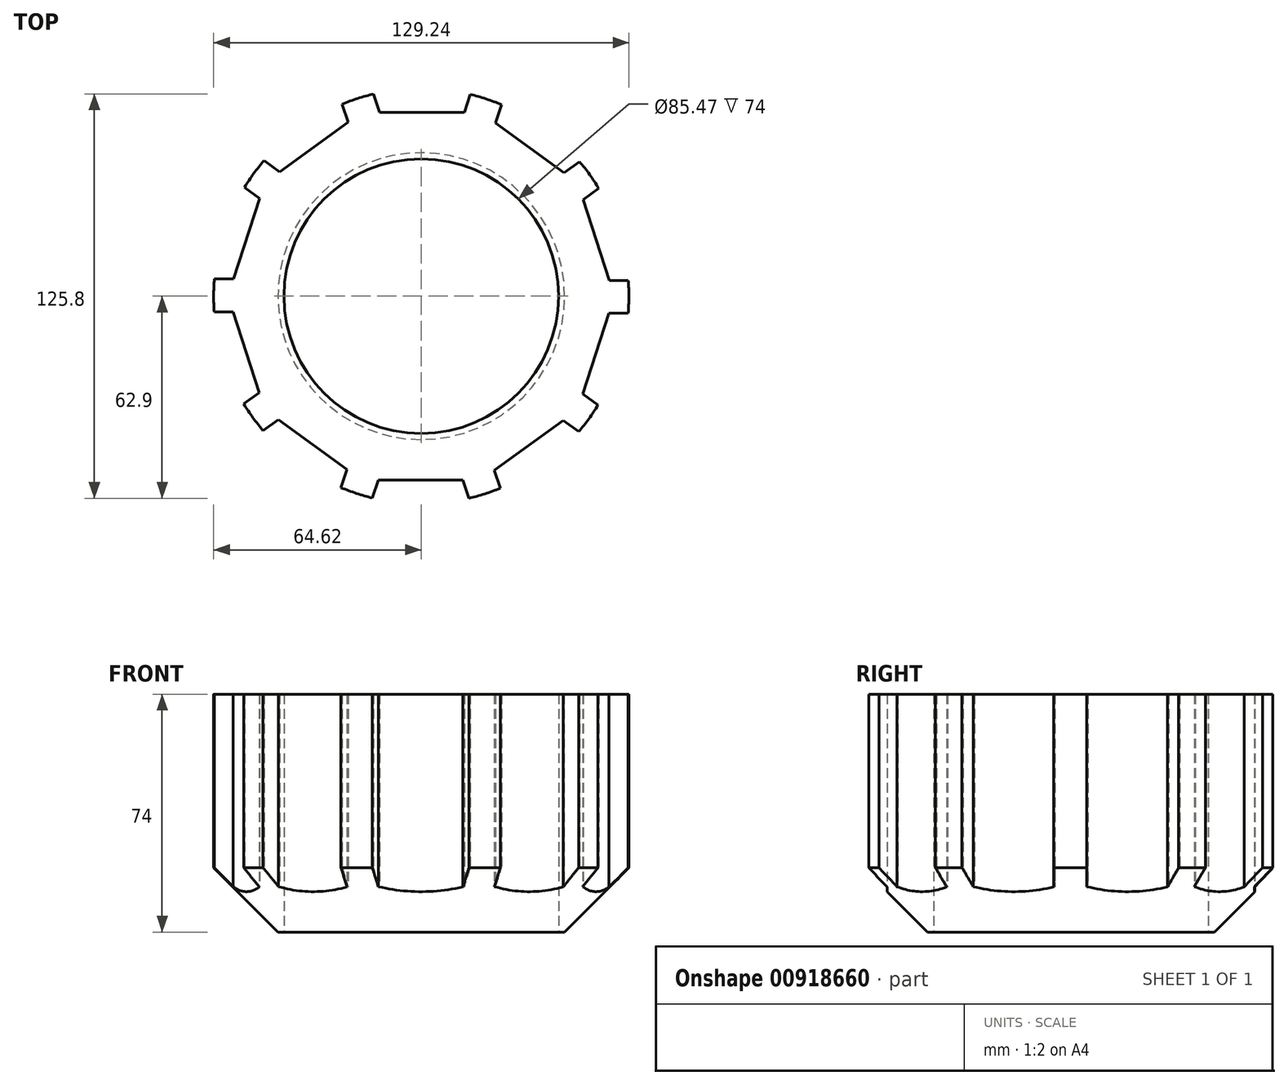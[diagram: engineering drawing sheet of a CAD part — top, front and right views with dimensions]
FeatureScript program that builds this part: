
annotation { "Feature Type Name" : "Feature", "Feature Type Description" : "" }
export const myFeature = defineFeature(function(context is Context, id is Id, definition is map)
    precondition{}
    {
        {
            var Q0;
            Q0=qCreatedBy(makeId("Top.planeOp"),FACE);
            var sketch = newSketch(context, id + "F0", { "sketchPlane" : qUnion([Q0])});
            skCircle(sketch, "E0", {"center": v(0, 0) * mm, "radius": 64.62 * mm});
            skSolve(sketch);
        }
        {
            var Q0;
            Q0=qCreatedBy(makeId("Top.planeOp"),FACE);
            var sketch = newSketch(context, id + "F1", { "sketchPlane" : qUnion([Q0])});
            skCircle(sketch, "E1", {"center": v(0, 0) * mm, "radius": 42.74 * mm});
            skSolve(sketch);
        }
        {
            var Q0;
            Q0 = qSketchRegion(id + "F0", true);
            extrude(context, id + "F2", {"entities" : qUnion([Q0]), "depth" : 74 * mm, "offsetDistance" : 25 * mm});
        }
        {
            var Q0;
            Q0 = qSketchRegion(id + "F1", true);
            extrude(context, id + "F3", {"entities" : qUnion([Q0]), "operationType" : NewBodyOperationType.REMOVE, "endBound" : BoundingType.THROUGH_ALL, "depth" : 59 * mm, "offsetDistance" : 25 * mm});
        }
        {
            var Q0;
            Q0=makeQuery(id+"F2.opExtrude","CAP_EDGE",EDGE,{"disambiguationData":[OSD([sQuery(id+"F0.wireOp",EDGE,"E0")])],"isStart":true});
            chamfer(context, id + "F4", {"entities" : qUnion([Q0]), "width" : 20 * mm, "tangentPropagation" : true});
        }
        {
            var Q0;
            Q0=qCreatedBy(makeId("Top.planeOp"),FACE);
            var sketch = newSketch(context, id + "F5", { "sketchPlane" : qUnion([Q0])});
            skCircle(sketch, "E2.cCircle", {"center": v(-0.22, -75.35) * mm, "radius": 22.44 * mm, "construction": true});
            skLineSegment(sketch, "E2.0", {"start": v(-0.25, -97.78) * mm, "end": v(-21.57, -82.26) * mm});
            skLineSegment(sketch, "E2.1", {"start": v(-21.57, -82.26) * mm, "end": v(-13.4, -57.18) * mm});
            skLineSegment(sketch, "E2.2", {"start": v(-13.4, -57.18) * mm, "end": v(12.98, -57.2) * mm});
            skLineSegment(sketch, "E2.3", {"start": v(12.98, -57.2) * mm, "end": v(21.1, -82.3) * mm});
            skLineSegment(sketch, "E2.4", {"start": v(21.1, -82.3) * mm, "end": v(-0.25, -97.78) * mm});
            skLineSegment(sketch, "E3.1.0", {"start": v(30.9, -79.23) * mm, "end": v(22.78, -54.13) * mm});
            skCircle(sketch, "E3.1.1", {"center": v(44.1, -61.09) * mm, "radius": 22.44 * mm, "construction": true});
            skLineSegment(sketch, "E3.1.2", {"start": v(44.13, -38.65) * mm, "end": v(65.45, -54.18) * mm});
            skLineSegment(sketch, "E3.1.3", {"start": v(57.28, -79.25) * mm, "end": v(30.9, -79.23) * mm});
            skLineSegment(sketch, "E3.1.4", {"start": v(22.78, -54.13) * mm, "end": v(44.13, -38.65) * mm});
            skLineSegment(sketch, "E3.1.5", {"start": v(65.45, -54.18) * mm, "end": v(57.28, -79.25) * mm});
            skLineSegment(sketch, "E3.2.0", {"start": v(71.57, -45.93) * mm, "end": v(50.24, -30.4) * mm});
            skCircle(sketch, "E3.2.1", {"center": v(71.6, -23.5) * mm, "radius": 22.44 * mm, "construction": true});
            skLineSegment(sketch, "E3.2.2", {"start": v(58.42, -5.33) * mm, "end": v(84.8, -5.36) * mm});
            skLineSegment(sketch, "E3.2.3", {"start": v(92.92, -30.45) * mm, "end": v(71.57, -45.93) * mm});
            skLineSegment(sketch, "E3.2.4", {"start": v(50.24, -30.4) * mm, "end": v(58.42, -5.33) * mm});
            skLineSegment(sketch, "E3.2.5", {"start": v(84.8, -5.36) * mm, "end": v(92.92, -30.45) * mm});
            skLineSegment(sketch, "E3.3.0", {"start": v(84.9, 4.9) * mm, "end": v(58.52, 4.93) * mm});
            skCircle(sketch, "E3.3.1", {"center": v(71.73, 23.07) * mm, "radius": 22.44 * mm, "construction": true});
            skLineSegment(sketch, "E3.3.2", {"start": v(50.4, 30.03) * mm, "end": v(71.75, 45.5) * mm});
            skLineSegment(sketch, "E3.3.3", {"start": v(93.07, 29.98) * mm, "end": v(84.9, 4.9) * mm});
            skLineSegment(sketch, "E3.3.4", {"start": v(58.52, 4.93) * mm, "end": v(50.4, 30.03) * mm});
            skLineSegment(sketch, "E3.3.5", {"start": v(71.75, 45.5) * mm, "end": v(93.07, 29.98) * mm});
            skLineSegment(sketch, "E3.4.0", {"start": v(65.8, 53.87) * mm, "end": v(44.45, 38.39) * mm});
            skCircle(sketch, "E3.4.1", {"center": v(44.47, 60.83) * mm, "radius": 22.44 * mm, "construction": true});
            skLineSegment(sketch, "E3.4.2", {"start": v(23.12, 53.91) * mm, "end": v(31.3, 79) * mm});
            skLineSegment(sketch, "E3.4.3", {"start": v(57.67, 78.96) * mm, "end": v(65.8, 53.87) * mm});
            skLineSegment(sketch, "E3.4.4", {"start": v(44.45, 38.39) * mm, "end": v(23.12, 53.91) * mm});
            skLineSegment(sketch, "E3.4.5", {"start": v(31.3, 79) * mm, "end": v(57.67, 78.96) * mm});
            skLineSegment(sketch, "E3.5.0", {"start": v(21.57, 82.26) * mm, "end": v(13.4, 57.18) * mm});
            skCircle(sketch, "E3.5.1", {"center": v(0.22, 75.35) * mm, "radius": 22.44 * mm, "construction": true});
            skLineSegment(sketch, "E3.5.2", {"start": v(-12.98, 57.2) * mm, "end": v(-21.1, 82.3) * mm});
            skLineSegment(sketch, "E3.5.3", {"start": v(0.25, 97.78) * mm, "end": v(21.57, 82.26) * mm});
            skLineSegment(sketch, "E3.5.4", {"start": v(13.4, 57.18) * mm, "end": v(-12.98, 57.2) * mm});
            skLineSegment(sketch, "E3.5.5", {"start": v(-21.1, 82.3) * mm, "end": v(0.25, 97.78) * mm});
            skLineSegment(sketch, "E3.6.0", {"start": v(-30.9, 79.23) * mm, "end": v(-22.78, 54.13) * mm});
            skCircle(sketch, "E3.6.1", {"center": v(-44.1, 61.09) * mm, "radius": 22.44 * mm, "construction": true});
            skLineSegment(sketch, "E3.6.2", {"start": v(-44.13, 38.65) * mm, "end": v(-65.45, 54.18) * mm});
            skLineSegment(sketch, "E3.6.3", {"start": v(-57.28, 79.25) * mm, "end": v(-30.9, 79.23) * mm});
            skLineSegment(sketch, "E3.6.4", {"start": v(-22.78, 54.13) * mm, "end": v(-44.13, 38.65) * mm});
            skLineSegment(sketch, "E3.6.5", {"start": v(-65.45, 54.18) * mm, "end": v(-57.28, 79.25) * mm});
            skLineSegment(sketch, "E3.7.0", {"start": v(-71.57, 45.93) * mm, "end": v(-50.24, 30.4) * mm});
            skCircle(sketch, "E3.7.1", {"center": v(-71.6, 23.5) * mm, "radius": 22.44 * mm, "construction": true});
            skLineSegment(sketch, "E3.7.2", {"start": v(-58.42, 5.33) * mm, "end": v(-84.8, 5.36) * mm});
            skLineSegment(sketch, "E3.7.3", {"start": v(-92.92, 30.45) * mm, "end": v(-71.57, 45.93) * mm});
            skLineSegment(sketch, "E3.7.4", {"start": v(-50.24, 30.4) * mm, "end": v(-58.42, 5.33) * mm});
            skLineSegment(sketch, "E3.7.5", {"start": v(-84.8, 5.36) * mm, "end": v(-92.92, 30.45) * mm});
            skLineSegment(sketch, "E3.8.0", {"start": v(-84.9, -4.9) * mm, "end": v(-58.52, -4.93) * mm});
            skCircle(sketch, "E3.8.1", {"center": v(-71.73, -23.07) * mm, "radius": 22.44 * mm, "construction": true});
            skLineSegment(sketch, "E3.8.2", {"start": v(-50.4, -30.03) * mm, "end": v(-71.75, -45.5) * mm});
            skLineSegment(sketch, "E3.8.3", {"start": v(-93.07, -29.98) * mm, "end": v(-84.9, -4.9) * mm});
            skLineSegment(sketch, "E3.8.4", {"start": v(-58.52, -4.93) * mm, "end": v(-50.4, -30.03) * mm});
            skLineSegment(sketch, "E3.8.5", {"start": v(-71.75, -45.5) * mm, "end": v(-93.07, -29.98) * mm});
            skLineSegment(sketch, "E3.9.0", {"start": v(-65.8, -53.87) * mm, "end": v(-44.45, -38.39) * mm});
            skCircle(sketch, "E3.9.1", {"center": v(-44.47, -60.83) * mm, "radius": 22.44 * mm, "construction": true});
            skLineSegment(sketch, "E3.9.2", {"start": v(-23.12, -53.91) * mm, "end": v(-31.3, -79) * mm});
            skLineSegment(sketch, "E3.9.3", {"start": v(-57.67, -78.96) * mm, "end": v(-65.8, -53.87) * mm});
            skLineSegment(sketch, "E3.9.4", {"start": v(-44.45, -38.39) * mm, "end": v(-23.12, -53.91) * mm});
            skLineSegment(sketch, "E3.9.5", {"start": v(-31.3, -79) * mm, "end": v(-57.67, -78.96) * mm});
            skPoint(sketch, "E3.center", {"position": v(0, 0) * mm});
            skSolve(sketch);
        }
        {
            var Q0;
            Q0=makeQuery(id+"F5.imprint","IMPRINT",FACE,{"disambiguationData":[TD([[makeQuery(id+"F5.imprint","IMPRINT",EDGE,{"derivedFrom":sQuery(id+"F5.wireOp",EDGE,"E2.0")}),-1.0]])]});
            var Q1;
            Q1=makeQuery(id+"F5.imprint","IMPRINT",FACE,{"disambiguationData":[TD([[makeQuery(id+"F5.imprint","IMPRINT",EDGE,{"derivedFrom":sQuery(id+"F5.wireOp",EDGE,"E3.1.0")}),-1.0]])]});
            var Q2;
            Q2=makeQuery(id+"F5.imprint","IMPRINT",FACE,{"disambiguationData":[TD([[makeQuery(id+"F5.imprint","IMPRINT",EDGE,{"derivedFrom":sQuery(id+"F5.wireOp",EDGE,"E3.2.0")}),-1.0]])]});
            var Q3;
            Q3=makeQuery(id+"F5.imprint","IMPRINT",FACE,{"disambiguationData":[TD([[makeQuery(id+"F5.imprint","IMPRINT",EDGE,{"derivedFrom":sQuery(id+"F5.wireOp",EDGE,"E3.3.0")}),-1.0]])]});
            var Q4;
            Q4=makeQuery(id+"F5.imprint","IMPRINT",FACE,{"disambiguationData":[TD([[makeQuery(id+"F5.imprint","IMPRINT",EDGE,{"derivedFrom":sQuery(id+"F5.wireOp",EDGE,"E3.4.0")}),-1.0]])]});
            var Q5;
            Q5=makeQuery(id+"F5.imprint","IMPRINT",FACE,{"disambiguationData":[TD([[makeQuery(id+"F5.imprint","IMPRINT",EDGE,{"derivedFrom":sQuery(id+"F5.wireOp",EDGE,"E3.5.0")}),-1.0]])]});
            var Q6;
            Q6=makeQuery(id+"F5.imprint","IMPRINT",FACE,{"disambiguationData":[TD([[makeQuery(id+"F5.imprint","IMPRINT",EDGE,{"derivedFrom":sQuery(id+"F5.wireOp",EDGE,"E3.6.0")}),-1.0]])]});
            var Q7;
            Q7=makeQuery(id+"F5.imprint","IMPRINT",FACE,{"disambiguationData":[TD([[makeQuery(id+"F5.imprint","IMPRINT",EDGE,{"derivedFrom":sQuery(id+"F5.wireOp",EDGE,"E3.7.0")}),-1.0]])]});
            var Q8;
            Q8=makeQuery(id+"F5.imprint","IMPRINT",FACE,{"disambiguationData":[TD([[makeQuery(id+"F5.imprint","IMPRINT",EDGE,{"derivedFrom":sQuery(id+"F5.wireOp",EDGE,"E3.8.0")}),-1.0]])]});
            var Q9;
            Q9=makeQuery(id+"F5.imprint","IMPRINT",FACE,{"disambiguationData":[TD([[makeQuery(id+"F5.imprint","IMPRINT",EDGE,{"derivedFrom":sQuery(id+"F5.wireOp",EDGE,"E3.9.0")}),-1.0]])]});
            extrude(context, id + "F6", {"entities" : qUnion([Q0, Q1, Q2, Q3, Q4, Q5, Q6, Q7, Q8, Q9]), "operationType" : NewBodyOperationType.REMOVE, "depth" : 102 * mm, "offsetDistance" : 25 * mm});
        }
    });
